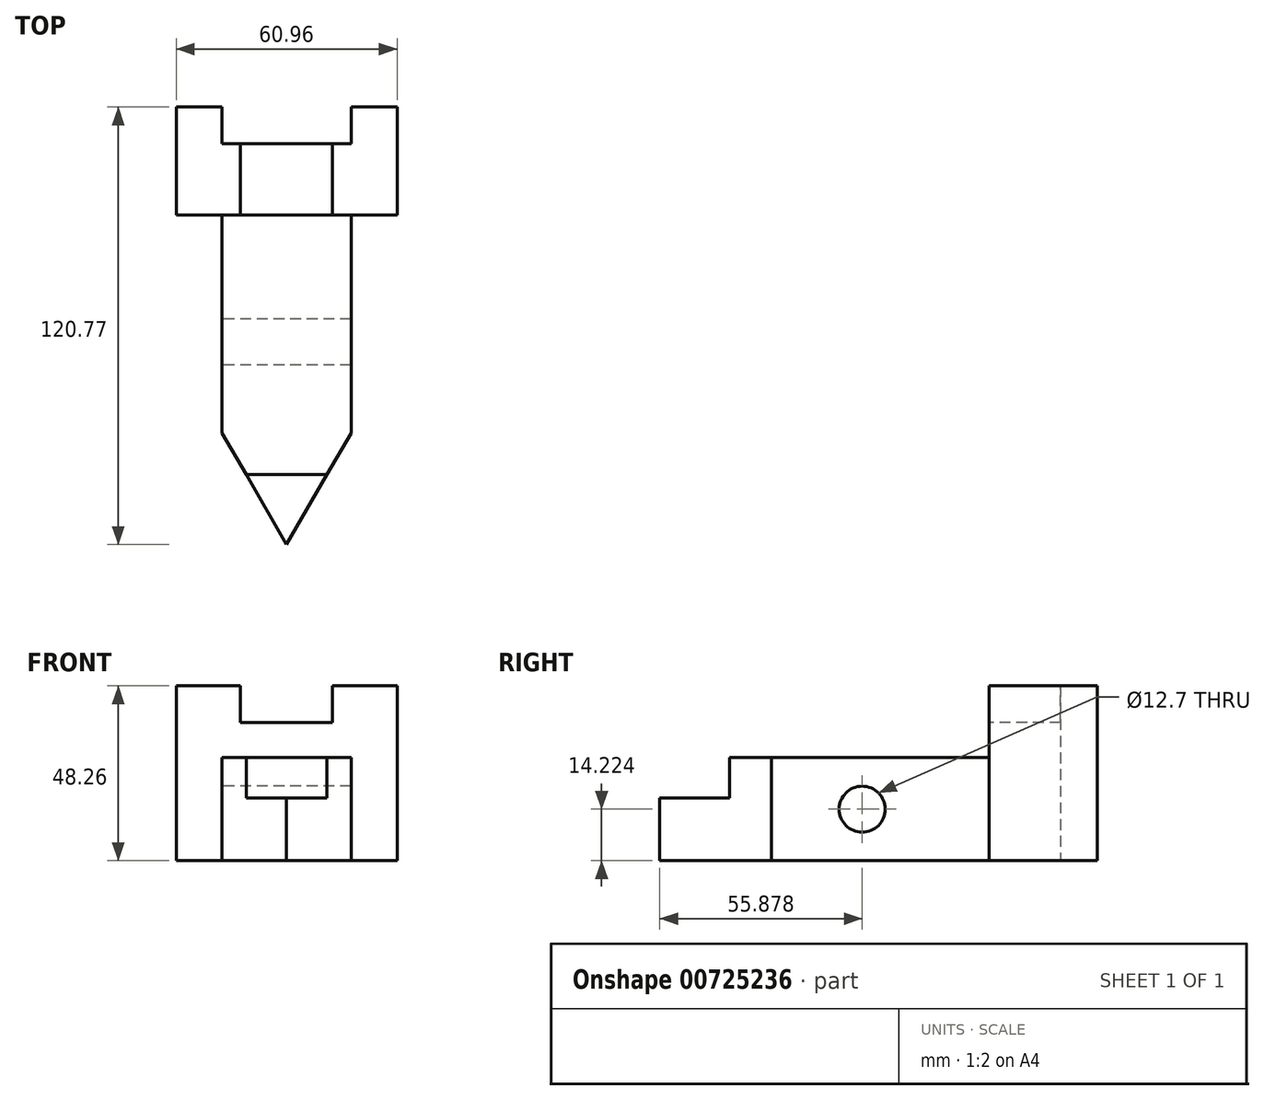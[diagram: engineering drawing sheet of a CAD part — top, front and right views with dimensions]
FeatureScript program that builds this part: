
annotation { "Feature Type Name" : "Feature", "Feature Type Description" : "" }
export const myFeature = defineFeature(function(context is Context, id is Id, definition is map)
    precondition{}
    {
        {
            var Q0;
            Q0=qCreatedBy(makeId("Top.planeOp"),FACE);
            var sketch = newSketch(context, id + "F0", { "sketchPlane" : qUnion([Q0])});
            skLineSegment(sketch, "E0.bottom", {"start": v(0, 0) * mm, "end": v(35.56, 0) * mm});
            skLineSegment(sketch, "E0.top", {"start": v(0, -90.93) * mm, "end": v(35.56, -90.93) * mm});
            skLineSegment(sketch, "E0.left", {"start": v(0, 0) * mm, "end": v(0, -90.93) * mm});
            skLineSegment(sketch, "E0.right", {"start": v(35.56, 0) * mm, "end": v(35.56, -90.93) * mm});
            skLineSegment(sketch, "E1", {"start": v(17.78, -90.93) * mm, "end": v(0, -60.14) * mm});
            skLineSegment(sketch, "E2", {"start": v(17.78, -90.93) * mm, "end": v(35.56, -60.14) * mm});
            skLineSegment(sketch, "E3.bottom", {"start": v(-12.7, 0) * mm, "end": v(48.26, 0) * mm});
            skLineSegment(sketch, "E3.top", {"start": v(-12.7, 29.84) * mm, "end": v(48.26, 29.84) * mm});
            skLineSegment(sketch, "E3.left", {"start": v(-12.7, 0) * mm, "end": v(-12.7, 29.84) * mm});
            skLineSegment(sketch, "E3.right", {"start": v(48.26, 0) * mm, "end": v(48.26, 29.84) * mm});
            skLineSegment(sketch, "E4.bottom", {"start": v(0, 29.84) * mm, "end": v(35.56, 29.84) * mm});
            skLineSegment(sketch, "E4.top", {"start": v(0, 19.68) * mm, "end": v(35.56, 19.68) * mm});
            skLineSegment(sketch, "E4.left", {"start": v(0, 29.84) * mm, "end": v(0, 19.68) * mm});
            skLineSegment(sketch, "E4.right", {"start": v(35.56, 29.84) * mm, "end": v(35.56, 19.68) * mm});
            skLineSegment(sketch, "E5", {"start": v(6.63, -71.63) * mm, "end": v(28.93, -71.63) * mm});
            skSolve(sketch);
        }
        {
            var Q0;
            {var subQ0=sQuery(id+"F0.wireOp",EDGE,"E3.left");Q0=makeQuery(id+"F0.imprint","IMPRINT",FACE,{"disambiguationData":[TD([[makeQuery(id+"F0.imprint","IMPRINT",EDGE,{"derivedFrom":subQ0}),-1.0]])]});}
            extrude(context, id + "F1", {"entities" : qUnion([Q0]), "depth" : 48.26 * mm, "offsetDistance" : 25.4 * mm});
        }
        {
            var Q0;
            {var subQ3=sQuery(id+"F0.wireOp",EDGE,"E5");Q0=makeQuery(id+"F0.imprint","IMPRINT",FACE,{"disambiguationData":[TD([[makeQuery(id+"F0.imprint","IMPRINT",EDGE,{"derivedFrom":subQ3}),1.0]])]});}
            extrude(context, id + "F2", {"entities" : qUnion([Q0]), "operationType" : NewBodyOperationType.ADD, "depth" : 28.45 * mm, "offsetDistance" : 25.4 * mm});
        }
        {
            var Q0;
            {var subQ3=sQuery(id+"F0.wireOp",EDGE,"E5");Q0=makeQuery(id+"F0.imprint","IMPRINT",FACE,{"disambiguationData":[TD([[makeQuery(id+"F0.imprint","IMPRINT",EDGE,{"derivedFrom":subQ3}),-1.0]])]});}
            extrude(context, id + "F3", {"entities" : qUnion([Q0]), "operationType" : NewBodyOperationType.ADD, "depth" : 17.27 * mm, "offsetDistance" : 25.4 * mm});
        }
        {
            var Q0;
            Q0=makeQuery(id+"F1.opExtrude","SWEPT_FACE",FACE,{"disambiguationData":[OSD([sQuery(id+"F0.wireOp",EDGE,"E3.bottom")])]});
            var sketch = newSketch(context, id + "F4", { "sketchPlane" : qUnion([Q0])});
            skLineSegment(sketch, "E6.bottom", {"start": v(30.48, 48.26) * mm, "end": v(5.08, 48.26) * mm});
            skLineSegment(sketch, "E6.top", {"start": v(30.48, 38.1) * mm, "end": v(5.08, 38.1) * mm});
            skLineSegment(sketch, "E6.left", {"start": v(30.48, 48.26) * mm, "end": v(30.48, 38.1) * mm});
            skLineSegment(sketch, "E6.right", {"start": v(5.08, 48.26) * mm, "end": v(5.08, 38.1) * mm});
            skPoint(sketch, "E6.middle", {"position": v(17.78, 43.18) * mm});
            skPoint(sketch, "E6.middle.positionSnap0", {"position": v(17.78, 48.26) * mm});
            skPoint(sketch, "E6.centerSnap0", {"position": v(17.78, 48.26) * mm});
            skSolve(sketch);
        }
        {
            var Q0;
            Q0=makeQuery(id+"F4.imprint","IMPRINT",FACE,{"disambiguationData":[TD([[makeQuery(id+"F4.imprint","IMPRINT",EDGE,{"derivedFrom":sQuery(id+"F4.wireOp",EDGE,"E6.bottom")}),-1.0]])]});
            extrude(context, id + "F5", {"entities" : qUnion([Q0]), "operationType" : NewBodyOperationType.REMOVE, "oppositeDirection" : true, "depth" : 25.4 * mm, "offsetDistance" : 25.4 * mm});
        }
        {
            var Q0;
            Q0=makeQuery(id+"F2.opExtrude","SWEPT_FACE",FACE,{"disambiguationData":[OSD([sQuery(id+"F0.wireOp",EDGE,"E0.left")])]});
            var sketch = newSketch(context, id + "F6", { "sketchPlane" : qUnion([Q0])});
            skCircle(sketch, "E7", {"center": v(35.05, 14.22) * mm, "radius": 6.35 * mm});
            skSolve(sketch);
        }
        {
            var Q0;
            Q0=makeQuery(id+"F6.imprint","IMPRINT",FACE,{"disambiguationData":[TD([[makeQuery(id+"F6.imprint","IMPRINT",EDGE,{"derivedFrom":sQuery(id+"F6.wireOp",EDGE,"E7")}),1.0]])]});
            extrude(context, id + "F7", {"entities" : qUnion([Q0]), "operationType" : NewBodyOperationType.REMOVE, "endBound" : BoundingType.THROUGH_ALL, "oppositeDirection" : true, "depth" : 25.4 * mm, "offsetDistance" : 25.4 * mm});
        }
    });
